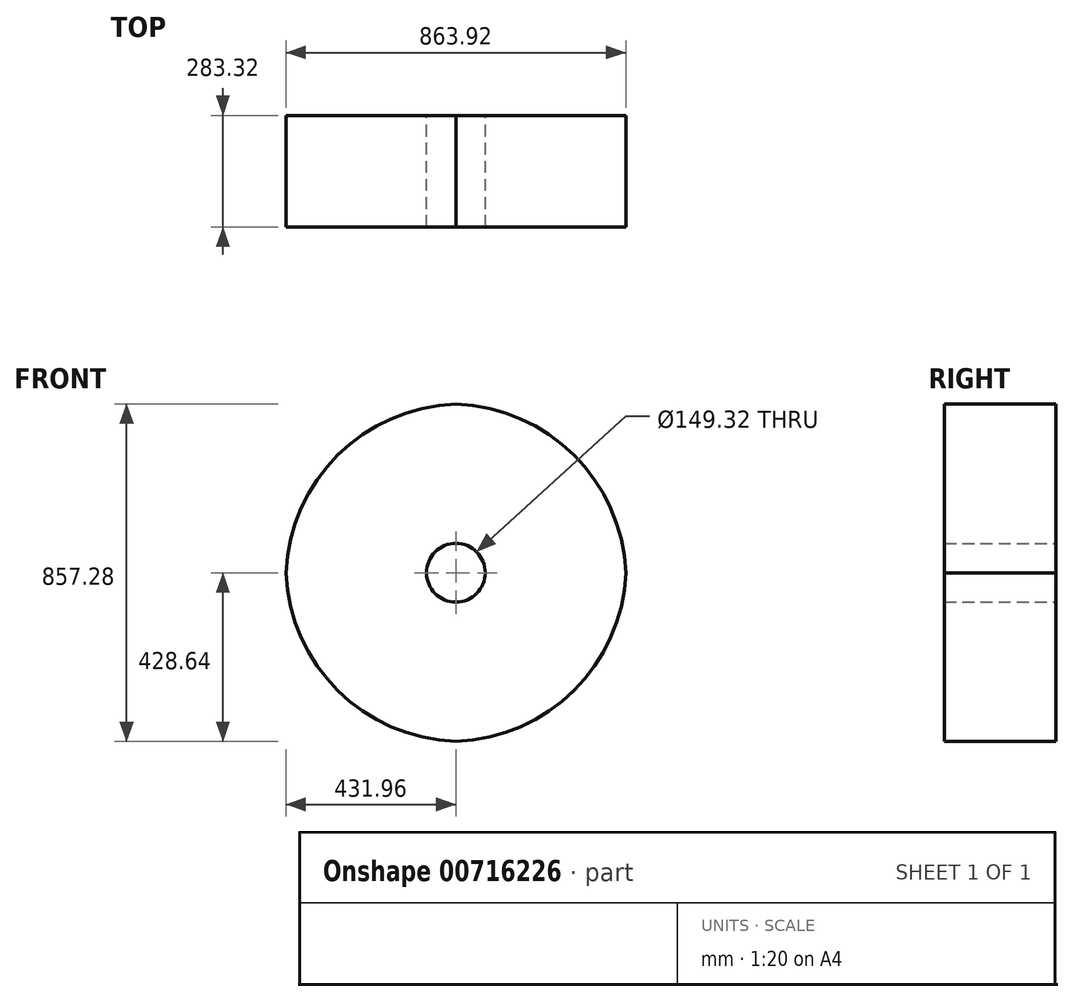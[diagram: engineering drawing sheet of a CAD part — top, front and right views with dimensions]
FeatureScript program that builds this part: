
annotation { "Feature Type Name" : "Feature", "Feature Type Description" : "" }
export const myFeature = defineFeature(function(context is Context, id is Id, definition is map)
    precondition{}
    {
        {
            var Q0;
            Q0=qCreatedBy(makeId("Front.planeOp"),FACE);
            var sketch = newSketch(context, id + "F0", { "sketchPlane" : qUnion([Q0])});
            skLineSegment(sketch, "E0.bottom", {"start": v(432.35, 428.9) * mm, "end": v(-432.35, 428.9) * mm});
            skLineSegment(sketch, "E0.top", {"start": v(432.35, -428.9) * mm, "end": v(-432.35, -428.9) * mm});
            skLineSegment(sketch, "E0.left", {"start": v(432.35, 428.9) * mm, "end": v(432.35, -428.9) * mm});
            skLineSegment(sketch, "E0.right", {"start": v(-432.35, 428.9) * mm, "end": v(-432.35, -428.9) * mm});
            skPoint(sketch, "E0.middle", {"position": v(0, 0) * mm});
            skCircle(sketch, "E1", {"center": v(0, 0) * mm, "radius": 74.66 * mm});
            skSolve(sketch);
        }
        {
            var Q0;
            Q0=makeQuery(id+"F0.imprint","IMPRINT",FACE,{"disambiguationData":[TD([[makeQuery(id+"F0.imprint","IMPRINT",EDGE,{"derivedFrom":sQuery(id+"F0.wireOp",EDGE,"E0.bottom")}),1.0]])]});
            var sketch = newSketch(context, id + "F1", { "sketchPlane" : qUnion([Q0])});
            skSolve(sketch);
        }
        {
            var Q0;
            Q0=makeQuery(id+"F1.imprint","IMPRINT",FACE,{"disambiguationData":[TD([[makeQuery(id+"F1.imprint","IMPRINT",EDGE,{"derivedFrom":makeQuery(id+"F0.imprint","IMPRINT",EDGE,{"derivedFrom":sQuery(id+"F0.wireOp",EDGE,"E0.bottom")})}),1.0]])]});
            extrude(context, id + "F2", {"entities" : qUnion([Q0]), "endBound" : BoundingType.SYMMETRIC, "depth" : 283.3 * mm, "offsetDistance" : 25.4 * mm});
        }
        {
            var Q0;
            Q0=makeQuery(id+"F2.opExtrude","SWEPT_EDGE",EDGE,{"disambiguationData":[OSD([sQuery(id+"F0.wireOp",EDGE,"E0.bottom"),sQuery(id+"F0.wireOp",EDGE,"E0.left")])]});
            var Q1;
            Q1=makeQuery(id+"F2.opExtrude","SWEPT_EDGE",EDGE,{"disambiguationData":[OSD([sQuery(id+"F0.wireOp",EDGE,"E0.top"),sQuery(id+"F0.wireOp",EDGE,"E0.left")])]});
            var Q2;
            Q2=makeQuery(id+"F2.opExtrude","SWEPT_EDGE",EDGE,{"disambiguationData":[OSD([sQuery(id+"F0.wireOp",EDGE,"E0.top"),sQuery(id+"F0.wireOp",EDGE,"E0.right")])]});
            var Q3;
            Q3=makeQuery(id+"F2.opExtrude","SWEPT_EDGE",EDGE,{"disambiguationData":[OSD([sQuery(id+"F0.wireOp",EDGE,"E0.bottom"),sQuery(id+"F0.wireOp",EDGE,"E0.right")])]});
            fillet(context, id + "F3", {"entities" : qUnion([Q0, Q1, Q2, Q3]), "radius" : 447.64 * mm, "tangentPropagation" : true, "allowEdgeOverflow" : false});
        }
    });
